# Revit family: PA_Арматура трубопроводов [кран шаровой латунный с переходом на полипропиленовую трубу VTp.742.0] - VALTEC
name_source: partatom
category: Арматура трубопроводов
units: mm (PartAtom-declared; Revit-internal decimal feet)

## family parameters
Всегда вертикально = Да
На основе рабочей плоскости = Нет
Общий = Нет
При загрузке вырезать с полостями = Нет
Размер круглого соединителя = Использовать диаметр
Тип детали = Клапан - Вставляется

## types (4) — shared parameters
ADSK_URL документации изделия = https://valtec.ru
ADSK_URL страницы изделия = https://valtec.ru
ADSK_Материал = Сталь, нержавеющая - VALTEC
URL = https://valtec.ru
a3 = 1 мм
Материал доп.1 = Белый - VALTEC
Таблица = PA_Арматура трубопроводов [кран шаровой латунный с переходом на полипропиленовую трубу VTp.742.0] - VALTEC

## per-type parameters (varying)
- 20 х 1/2": A=65 мм; B=36 мм; C=91 мм; D1=15 мм; D2=20 мм; S1=37 мм; S2=25 мм; a1=9 мм; a2=12 мм; a4=2 мм; a5=11 мм; a6=2 мм; a7=1 мм; a8=14 мм; a9=2 мм; b1=16 мм; b2=1 мм; b3=11 мм; b4=2 мм; b5=2 мм; b6=5 мм; b7=7 мм; d1=28 мм; d2=25 мм; d3=30 мм; d4=15 мм; d5=14 мм; d6=8 мм; d7=12 мм; dn=27 мм; h=20 мм
- 25 х 3/4": A=73 мм; B=42 мм; C=91 мм; D1=20 мм; D2=25 мм; S1=46 мм; S2=31 мм; a1=11 мм; a2=13 мм; a4=2 мм; a5=12 мм; a6=2 мм; a7=1 мм; a8=15 мм; a9=3 мм; b1=19 мм; b2=1 мм; b3=13 мм; b4=2 мм; b5=3 мм; b6=6 мм; b7=8 мм; d1=34 мм; d2=31 мм; d3=38 мм; d4=19 мм; d5=17 мм; d6=10 мм; d7=15 мм; dn=33 мм; h=25 мм
- 32 х 1": A=83 мм; B=50 мм; C=116 мм; D1=25 мм; D2=32 мм; S1=56 мм; S2=37 мм; a1=12 мм; a2=15 мм; a4=3 мм; a5=13 мм; a6=2 мм; a7=1 мм; a8=18 мм; a9=3 мм; b1=22 мм; b2=2 мм; b3=15 мм; b4=3 мм; b5=3 мм; b6=7 мм; b7=9 мм; d1=42 мм; d2=37 мм; d3=46 мм; d4=23 мм; d5=21 мм; d6=12 мм; d7=18 мм; dn=43 мм; h=31 мм
- 40 х 1 1/4": A=100 мм; B=60 мм; C=116 мм; D1=32 мм; D2=40 мм; S1=64 мм; S2=42 мм; a1=14 мм; a2=18 мм; a4=3 мм; a5=16 мм; a6=3 мм; a7=2 мм; a8=21 мм; a9=4 мм; b1=27 мм; b2=2 мм; b3=19 мм; b4=3 мм; b5=4 мм; b6=9 мм; b7=11 мм; d1=48 мм; d2=43 мм; d3=53 мм; d4=27 мм; d5=24 мм; d6=14 мм; d7=20 мм; dn=53 мм; h=35 мм
